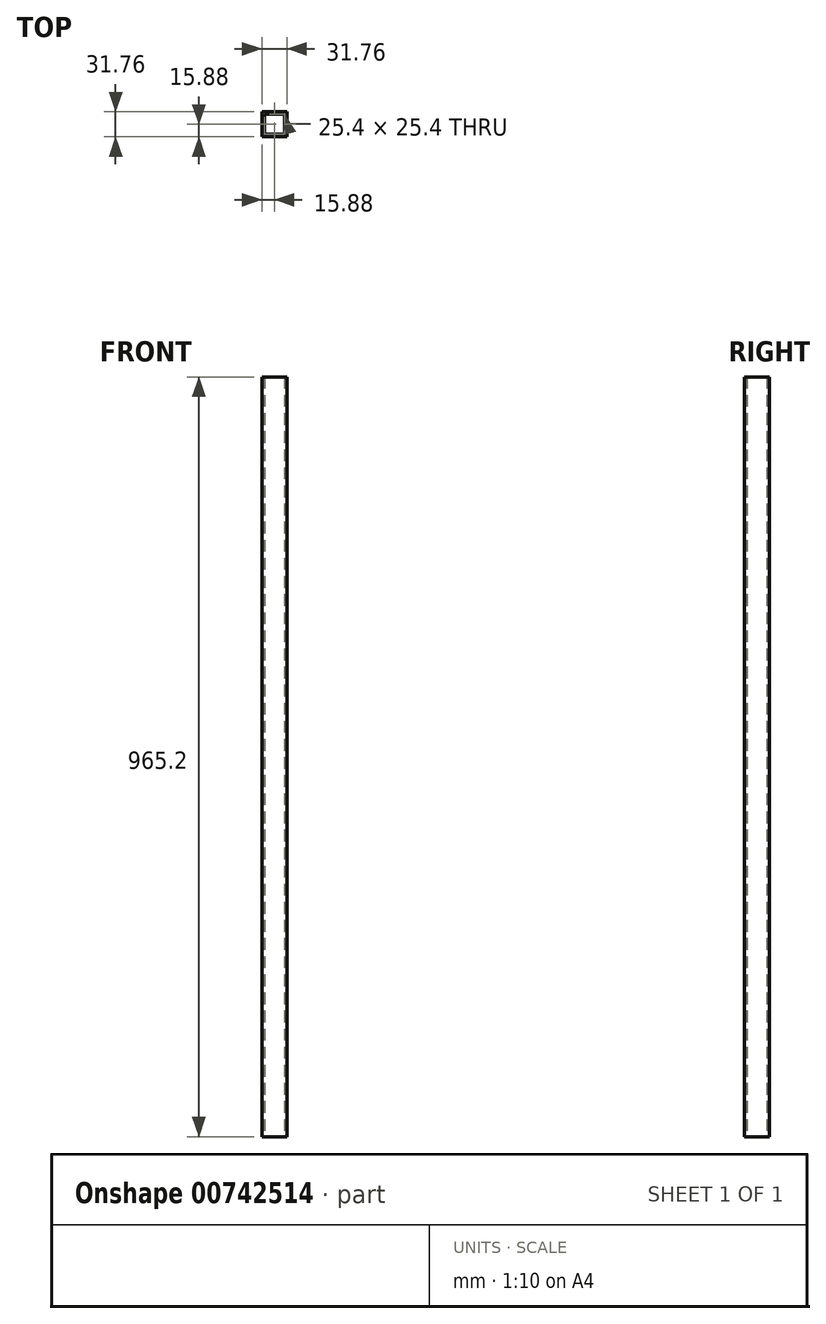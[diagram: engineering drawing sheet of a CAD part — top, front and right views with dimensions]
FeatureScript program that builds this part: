
annotation { "Feature Type Name" : "Feature", "Feature Type Description" : "" }
export const myFeature = defineFeature(function(context is Context, id is Id, definition is map)
    precondition{}
    {
        {
            var Q0;
            Q0=qCreatedBy(makeId("Top.planeOp"),FACE);
            var sketch = newSketch(context, id + "F0", { "sketchPlane" : qUnion([Q0])});
            skLineSegment(sketch, "E0.bottom", {"start": v(12.7, 12.7) * mm, "end": v(-12.7, 12.7) * mm});
            skLineSegment(sketch, "E0.top", {"start": v(12.7, -12.7) * mm, "end": v(-12.7, -12.7) * mm});
            skLineSegment(sketch, "E0.left", {"start": v(12.7, 12.7) * mm, "end": v(12.7, -12.7) * mm});
            skLineSegment(sketch, "E0.right", {"start": v(-12.7, 12.7) * mm, "end": v(-12.7, -12.7) * mm});
            skPoint(sketch, "E0.middle", {"position": v(0, 0) * mm});
            skLineSegment(sketch, "E1.0", {"start": v(15.88, -15.88) * mm, "end": v(-15.88, -15.88) * mm});
            skLineSegment(sketch, "E1.1", {"start": v(15.88, 15.88) * mm, "end": v(15.88, -15.88) * mm});
            skLineSegment(sketch, "E1.2", {"start": v(15.88, 15.88) * mm, "end": v(-15.88, 15.88) * mm});
            skLineSegment(sketch, "E1.3", {"start": v(-15.88, 15.88) * mm, "end": v(-15.88, -15.88) * mm});
            skSolve(sketch);
        }
        {
            var Q0;
            Q0=qSketchRegion(id+"F0",true);
            extrude(context, id + "F1", {"entities" : qUnion([Q0]), "depth" : 965.2 * mm, "offsetDistance" : 25.4 * mm});
        }
        {
            var Q0;
            Q0=makeQuery(id+"F1.opExtrude","CAP_FACE",FACE,{"disambiguationData":[OSD([sQuery(id+"F0.wireOp",EDGE,"E0.bottom"),sQuery(id+"F0.wireOp",EDGE,"E0.top"),sQuery(id+"F0.wireOp",EDGE,"E0.left"),sQuery(id+"F0.wireOp",EDGE,"E0.right"),sQuery(id+"F0.wireOp",EDGE,"E1.0"),sQuery(id+"F0.wireOp",EDGE,"E1.1"),sQuery(id+"F0.wireOp",EDGE,"E1.2"),sQuery(id+"F0.wireOp",EDGE,"E1.3")])],"isStart":false});
            var sketch = newSketch(context, id + "F2", { "sketchPlane" : qUnion([Q0])});
            skLineSegment(sketch, "E2", {"start": v(-15.88, 15.88) * mm, "end": v(15.88, -15.88) * mm, "construction": true});
            skSolve(sketch);
        }
    });
